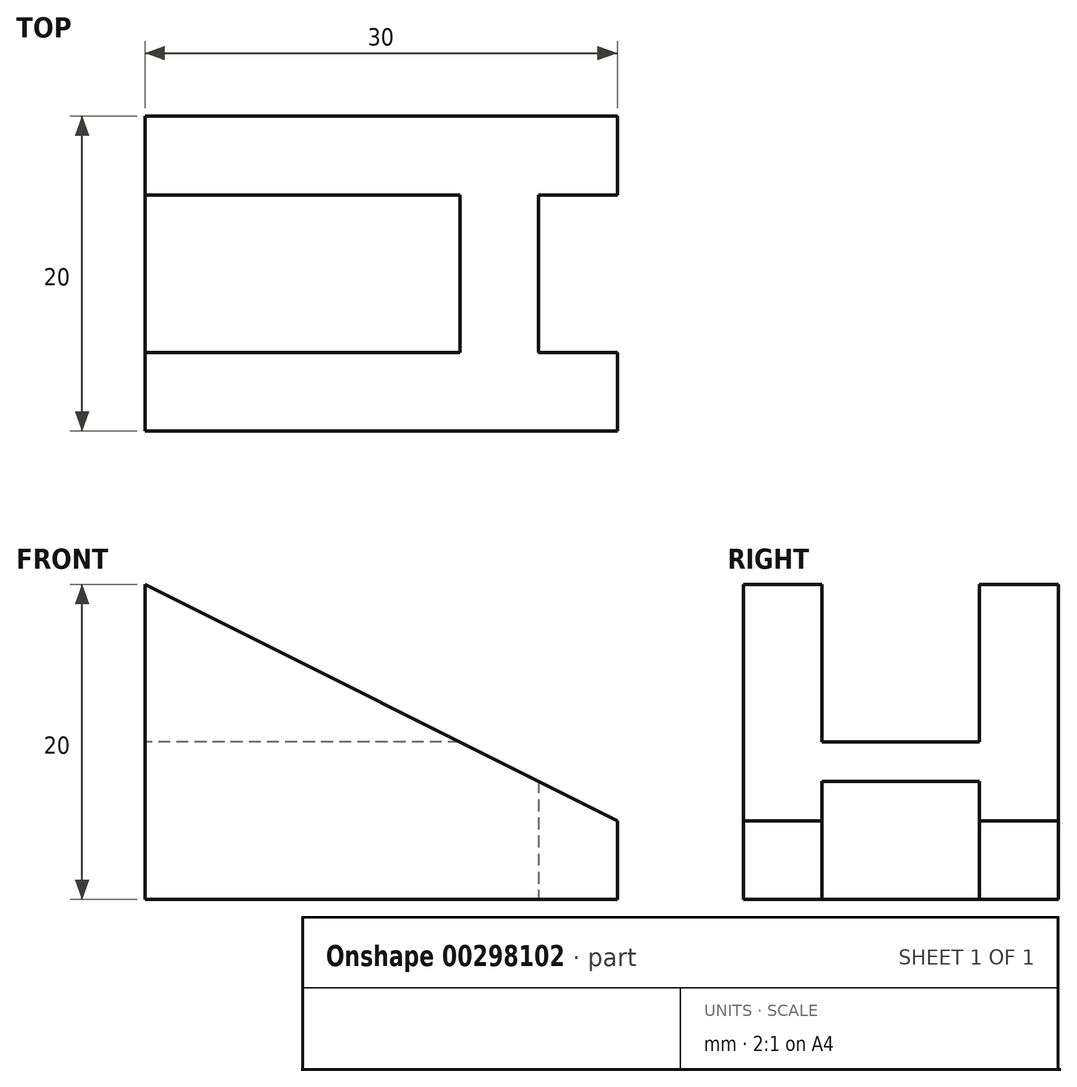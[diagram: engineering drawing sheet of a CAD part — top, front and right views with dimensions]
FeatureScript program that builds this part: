
annotation { "Feature Type Name" : "Feature", "Feature Type Description" : "" }
export const myFeature = defineFeature(function(context is Context, id is Id, definition is map)
    precondition{}
    {
        {
            var Q0;
            Q0=qCreatedBy(makeId("Front.planeOp"),FACE);
            var sketch = newSketch(context, id + "F0", { "sketchPlane" : qUnion([Q0])});
            skLineSegment(sketch, "E0", {"start": v(0, 0) * mm, "end": v(30, 0) * mm});
            skLineSegment(sketch, "E1", {"start": v(30, 0) * mm, "end": v(30, 5) * mm});
            skLineSegment(sketch, "E2", {"start": v(30, 5) * mm, "end": v(0, 20) * mm});
            skLineSegment(sketch, "E3", {"start": v(0, 20) * mm, "end": v(0, 0) * mm});
            skSolve(sketch);
        }
        {
            var Q0;
            Q0=makeQuery(id+"F0.imprint","IMPRINT",FACE,{"disambiguationData":[TD([[makeQuery(id+"F0.imprint","IMPRINT",EDGE,{"derivedFrom":sQuery(id+"F0.wireOp",EDGE,"E0")}),1.0]])]});
            extrude(context, id + "F1", {"entities" : qUnion([Q0]), "endBound" : BoundingType.SYMMETRIC, "depth" : 20 * mm});
        }
        {
            var Q0;
            Q0=makeQuery(id+"F1.opExtrude","SWEPT_FACE",FACE,{"disambiguationData":[OSD([sQuery(id+"F0.wireOp",EDGE,"E3")])]});
            var sketch = newSketch(context, id + "F2", { "sketchPlane" : qUnion([Q0])});
            skLineSegment(sketch, "E4", {"start": v(0, 20) * mm, "end": v(5, 20) * mm});
            skLineSegment(sketch, "E5", {"start": v(5, 20) * mm, "end": v(5, 10) * mm});
            skLineSegment(sketch, "E6", {"start": v(5, 10) * mm, "end": v(0, 10) * mm});
            skLineSegment(sketch, "E7", {"start": v(0, 10) * mm, "end": v(-5, 10) * mm});
            skLineSegment(sketch, "E8", {"start": v(-5, 10) * mm, "end": v(-5, 20) * mm});
            skLineSegment(sketch, "E9", {"start": v(-5, 20) * mm, "end": v(0, 20) * mm});
            skSolve(sketch);
        }
        {
            var Q0;
            Q0=makeQuery(id+"F2.imprint","IMPRINT",FACE,{"disambiguationData":[TD([[makeQuery(id+"F2.imprint","IMPRINT",EDGE,{"derivedFrom":sQuery(id+"F2.wireOp",EDGE,"E4")}),1.0]])]});
            extrude(context, id + "F3", {"entities" : qUnion([Q0]), "operationType" : NewBodyOperationType.REMOVE, "endBound" : BoundingType.THROUGH_ALL, "oppositeDirection" : true, "depth" : 25 * mm});
        }
        {
            var Q0;
            Q0=makeQuery(id+"F1.opExtrude","SWEPT_FACE",FACE,{"disambiguationData":[OSD([sQuery(id+"F0.wireOp",EDGE,"E0")])]});
            var sketch = newSketch(context, id + "F4", { "sketchPlane" : qUnion([Q0])});
            skLineSegment(sketch, "E10", {"start": v(30, 0) * mm, "end": v(30, -5) * mm});
            skLineSegment(sketch, "E11", {"start": v(30, -5) * mm, "end": v(25, -5) * mm});
            skLineSegment(sketch, "E12", {"start": v(25, -5) * mm, "end": v(25, 0) * mm});
            skLineSegment(sketch, "E13", {"start": v(30, 0) * mm, "end": v(30, 5) * mm});
            skLineSegment(sketch, "E14", {"start": v(25, 5) * mm, "end": v(30, 5) * mm});
            skLineSegment(sketch, "E15", {"start": v(25, 0) * mm, "end": v(25, 5) * mm});
            skSolve(sketch);
        }
        {
            var Q0;
            Q0=makeQuery(id+"F4.imprint","IMPRINT",FACE,{"disambiguationData":[TD([[makeQuery(id+"F4.imprint","IMPRINT",EDGE,{"derivedFrom":sQuery(id+"F4.wireOp",EDGE,"E10")}),-1.0]])]});
            extrude(context, id + "F5", {"entities" : qUnion([Q0]), "operationType" : NewBodyOperationType.REMOVE, "oppositeDirection" : true, "depth" : 25 * mm});
        }
    });
